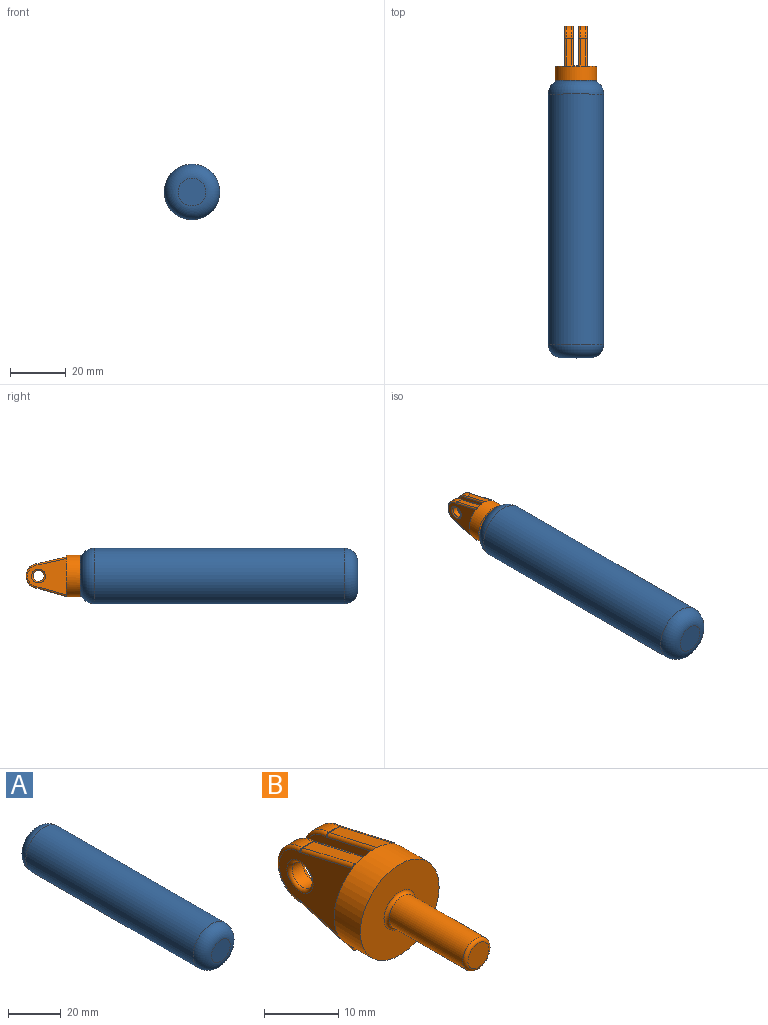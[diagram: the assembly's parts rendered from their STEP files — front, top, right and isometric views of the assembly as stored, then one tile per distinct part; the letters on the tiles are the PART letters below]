
ASSEMBLY  parts=2 mates=1
PART A: 7 faces, bbox 21.6x100x21.6 mm
  f0: cylinder r=10mm len=90mm, axis (0,1,0), area 5654.9mm2, adj f5,f6
  f1: plane 10x10mm, normal (0,-1,0), area 78.5mm2, adj f6
  f2: plane 10x10mm, normal (0,1,0), area 58.9mm2, adj f3,f5
  f3: cylinder r=2.5mm len=15mm, axis (0,1,0), area 235.6mm2, adj f2,f4
  f4: plane 5x5mm, normal (0,1,0), area 19.6mm2, adj f3
  f5: torus R=5mm, axis (0,-1,0), area 403.8mm2, adj f0,f2
  f6: torus R=5mm, axis (0,-1,0), area 403.8mm2, adj f0,f1
PART B: 54 faces, bbox 15x34.9x15.1 mm
  f0: plane 9.93x7mm, normal (0,0.28,-0.96), area 41.9mm2, adj f4,f14,f15,f20,f29,f33,f35,f36
  f1: cylinder r=4.5mm len=9mm, axis (-1,0,0), area 28mm2, adj f39,f40,f44,f45
  f2: cylinder r=2mm len=4mm, axis (-1,0,0), area 25.1mm2, adj f48,f51
  f3: plane 9.95x7mm, normal (0,0.23,0.97), area 41.1mm2, adj f9,f12,f13,f23,f24,f26,f27,f41
  f4: plane 2.61x0.11mm, normal (0,1,0), area 0.2mm2, adj f0,f7
  f5: plane 12.69x3.5mm, normal (0,1,0), area 31.3mm2, adj f7,f18,f41
  f6: plane 12.69x3.5mm, normal (0,1,0), area 31.3mm2, adj f7,f19,f24
  f7: cylinder r=7.5mm len=15mm, axis (0,1,0), area 235.6mm2, adj f4,f5,f6,f8,f9,f12,f13,f14
  f8: plane 15x15mm, normal (0,-1,0), area 148.4mm2, adj f7,f52
  f9: plane 6.27x0.69mm, normal (0,1,0), area 2.9mm2, adj f3,f7
  f10: cylinder r=2.5mm len=14mm, axis (0,1,0), area 219.9mm2, adj f52,f53
  f11: plane 4x4mm, normal (0,-1,0), area 12.6mm2, adj f53
  f12: plane 0.87x0.47mm, normal (0,-1,0), area 0.1mm2, adj f3,f7,f41
  f13: plane 0.87x0.47mm, normal (0,-1,0), area 0.1mm2, adj f3,f7,f24
  f14: plane 2.69x1.04mm, normal (0,-1,0), area 1.1mm2, adj f0,f7,f19,f29
  f15: plane 2.69x1.04mm, normal (0,-1,0), area 1.1mm2, adj f0,f7,f18,f36
  f16: cylinder r=4.5mm len=9mm, axis (-1,0,0), area 28mm2, adj f27,f28,f32,f33
  f17: cylinder r=2mm len=4mm, axis (-1,0,0), area 25.1mm2, adj f49,f50
  f18: plane 14x13.17mm, normal (1,0,0), area 111.2mm2, adj f5,f15,f36,f37,f40,f41,f43,f51
  f19: plane 14x13.17mm, normal (-1,0,0), area 111.2mm2, adj f6,f14,f24,f25,f28,f29,f31,f50
  f20: plane 3.19x3mm, normal (0,0.23,0.97), area 6.8mm2, adj f0,f21,f22,f23,f35,f38
  f21: plane 17.02x13.42mm, normal (-1,0,0), area 131.8mm2, adj f20,f23,f38,f42,f44,f46,f47,f48
  f22: plane 17.02x13.42mm, normal (1,0,0), area 131.8mm2, adj f20,f23,f26,f30,f32,f34,f35,f49
  f23: plane 13.4x3.1mm, normal (0,0.97,-0.23), area 27.6mm2, adj f3,f20,f21,f22,f26,f47
  f24: cylinder r=0.5mm len=10.06mm, axis (0,-0.97,0.23), area 8mm2, adj f3,f6,f13,f19,f25
  f25: torus R=1mm, axis (1,0,0), area 0.1mm2, adj f19,f24,f27,f28
  f26: cylinder r=0.5mm len=9.98mm, axis (0,0.97,-0.23), area 8mm2, adj f3,f22,f23,f30
  f27: cylinder r=0.5mm len=2mm, axis (-1,0,0), area 0.2mm2, adj f3,f16,f25,f30
  f28: torus R=4mm, axis (1,0,0), area 10.6mm2, adj f16,f19,f25,f31
  f29: cylinder r=0.5mm len=10.07mm, axis (0,0.96,0.28), area 8.1mm2, adj f0,f14,f19,f31
  f30: torus R=1mm, axis (-1,0,0), area 0.1mm2, adj f22,f26,f27,f32
  f31: torus R=1mm, axis (1,0,0), area 0.1mm2, adj f19,f28,f29,f33
  f32: torus R=4mm, axis (-1,0,0), area 10.6mm2, adj f16,f22,f30,f34
  f33: cylinder r=0.5mm len=2mm, axis (-1,0,0), area 0.3mm2, adj f0,f16,f31,f34
  f34: torus R=1mm, axis (-1,0,0), area 0.1mm2, adj f22,f32,f33,f35
  f35: cylinder r=0.5mm len=10.77mm, axis (0,-0.96,-0.28), area 8.2mm2, adj f0,f20,f22,f34
  f36: cylinder r=0.5mm len=10.07mm, axis (0,-0.96,-0.28), area 8.1mm2, adj f0,f15,f18,f37
  f37: torus R=1mm, axis (1,0,0), area 0.1mm2, adj f18,f36,f39,f40
  f38: cylinder r=0.5mm len=10.77mm, axis (0,0.96,0.28), area 8.2mm2, adj f0,f20,f21,f42
  f39: cylinder r=0.5mm len=2mm, axis (-1,0,0), area 0.3mm2, adj f0,f1,f37,f42
  f40: torus R=4mm, axis (1,0,0), area 10.6mm2, adj f1,f18,f37,f43
  f41: cylinder r=0.5mm len=10.06mm, axis (0,0.97,-0.23), area 8mm2, adj f3,f5,f12,f18,f43
  f42: torus R=1mm, axis (-1,0,0), area 0.1mm2, adj f21,f38,f39,f44
  f43: torus R=1mm, axis (1,0,0), area 0.1mm2, adj f18,f40,f41,f45
  f44: torus R=4mm, axis (-1,0,0), area 10.6mm2, adj f1,f21,f42,f46
  f45: cylinder r=0.5mm len=2mm, axis (-1,0,0), area 0.2mm2, adj f1,f3,f43,f46
  f46: torus R=1mm, axis (-1,0,0), area 0.1mm2, adj f21,f44,f45,f47
  f47: cylinder r=0.5mm len=9.98mm, axis (0,-0.97,0.23), area 8mm2, adj f3,f21,f23,f46
  f48: torus R=2.5mm, axis (-1,0,0), area 10.8mm2, adj f2,f21
  f49: torus R=2.5mm, axis (-1,0,0), area 10.8mm2, adj f17,f22
  f50: torus R=2.5mm, axis (1,0,0), area 10.8mm2, adj f17,f19
  f51: torus R=2.5mm, axis (1,0,0), area 10.8mm2, adj f2,f18
  f52: torus R=3mm, axis (0,-1,0), area 13.2mm2, adj f8,f10
  f53: torus R=2mm, axis (0,-1,0), area 11.4mm2, adj f10,f11
PLACE A t=(-24.9,53.46,-11.29)mm
PLACE B t=(-24.9,58.46,-11.29)mm
MATE revolute A.f0 <-> B.f7  axis (0,1,0) through (-24.9,45.96,-11.29)mm
